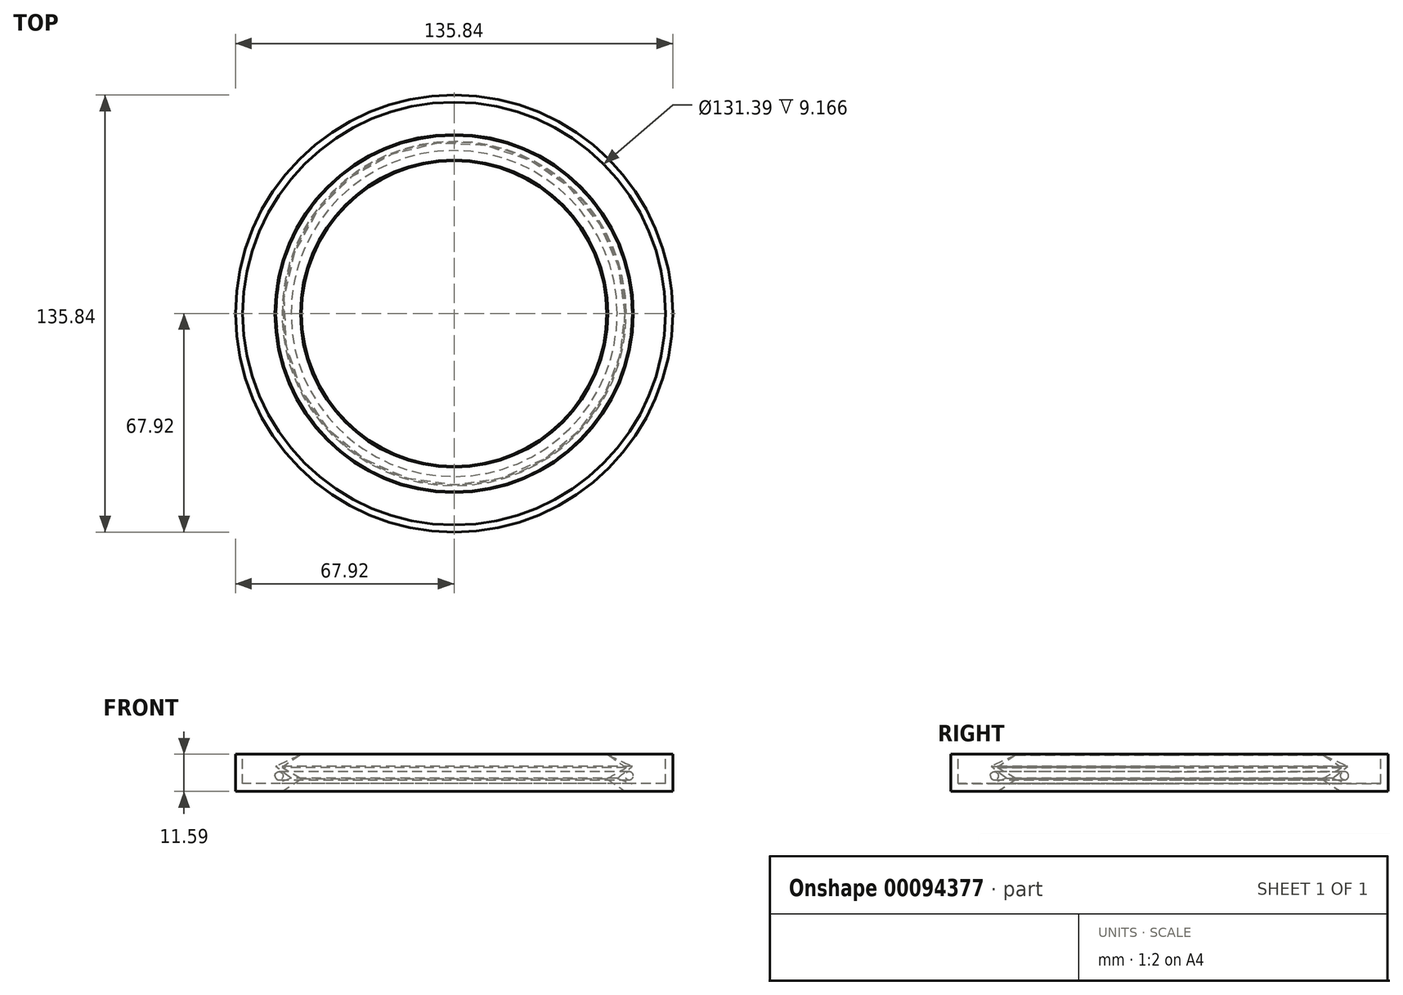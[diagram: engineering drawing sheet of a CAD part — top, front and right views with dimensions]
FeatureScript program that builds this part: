
annotation { "Feature Type Name" : "Feature", "Feature Type Description" : "" }
export const myFeature = defineFeature(function(context is Context, id is Id, definition is map)
    precondition{}
    {
        {
            var Q0;
            Q0=qCreatedBy(makeId("Front.planeOp"),FACE);
            var sketch = newSketch(context, id + "F0", { "sketchPlane" : qUnion([Q0])});
            skLineSegment(sketch, "E0", {"start": v(-67.92, 11.56) * mm, "end": v(-67.92, 0) * mm});
            skLineSegment(sketch, "E1", {"start": v(-67.92, 0) * mm, "end": v(-53.17, 0) * mm});
            skLineSegment(sketch, "E2", {"start": v(-53.17, 0) * mm, "end": v(-47.44, 3.9) * mm});
            skLineSegment(sketch, "E3", {"start": v(-47.44, 3.9) * mm, "end": v(-53.49, 7.39) * mm});
            skLineSegment(sketch, "E4", {"start": v(-53.49, 7.39) * mm, "end": v(-47.76, 11.38) * mm});
            skLineSegment(sketch, "E5", {"start": v(-47.76, 11.38) * mm, "end": v(-55.4, 7.77) * mm});
            skLineSegment(sketch, "E6", {"start": v(-55.4, 7.77) * mm, "end": v(-50.66, 4.07) * mm});
            skLineSegment(sketch, "E7", {"start": v(-50.66, 4.07) * mm, "end": v(-55.22, 2.43) * mm});
            skLineSegment(sketch, "E8", {"start": v(-55.22, 2.43) * mm, "end": v(-65.7, 2.43) * mm});
            skLineSegment(sketch, "E9", {"start": v(-65.7, 2.43) * mm, "end": v(-65.7, 11.6) * mm});
            skLineSegment(sketch, "E10", {"start": v(-65.7, 11.6) * mm, "end": v(-67.92, 11.56) * mm});
            skLineSegment(sketch, "E11", {"start": v(0, 42.41) * mm, "end": v(0, -20.28) * mm, "construction": true});
            skCircle(sketch, "E12", {"center": v(-54.41, 4.87) * mm, "radius": 1.26 * mm});
            skSolve(sketch);
        }
        {
            var Q0;
            Q0=makeQuery(id+"F0.imprint","IMPRINT",FACE,{"disambiguationData":[TD([[makeQuery(id+"F0.imprint","IMPRINT",EDGE,{"derivedFrom":sQuery(id+"F0.wireOp",EDGE,"E0")}),1.0]])]});
            var Q1;
            Q1=makeQuery(id+"F0.imprint","IMPRINT",FACE,{"disambiguationData":[TD([[makeQuery(id+"F0.imprint","IMPRINT",EDGE,{"derivedFrom":sQuery(id+"F0.wireOp",EDGE,"E12")}),1.0]])]});
            var Q2;
            Q2=sQuery(id+"F0.wireOp",EDGE,"E11");
            revolve(context, id + "F1", {"entities" : qUnion([Q0, Q1]), "axis" : qUnion([Q2]), "revolveType" : RevolveType.FULL});
        }
    });
